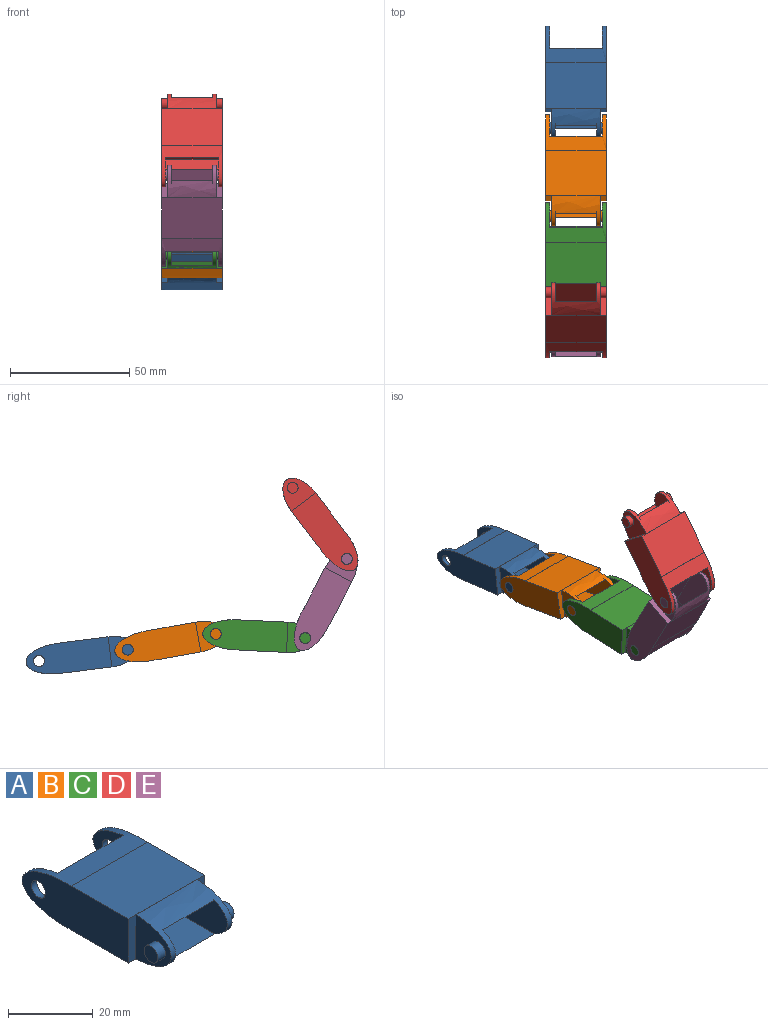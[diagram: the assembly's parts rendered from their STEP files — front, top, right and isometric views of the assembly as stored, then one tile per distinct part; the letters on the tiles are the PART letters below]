
ASSEMBLY  parts=5 mates=4
PART A: 27 faces, bbox 25.4x47.1x12.7 mm
  f0: plane 32.73x21.87mm, normal (0,0,-1), area 623.3mm2, adj f1,f3,f14,f15,f23,f24,f25,f26
  f1: plane 22.74x12.12mm, normal (1,0,0), area 196.9mm2, adj f0,f2,f7,f12,f13,f14,f26
  f2: plane 32.73x21.87mm, normal (0,0,1), area 623.3mm2, adj f1,f3,f13,f15,f23,f24,f25,f26
  f3: plane 22.74x12.12mm, normal (-1,0,0), area 196.9mm2, adj f0,f2,f6,f12,f13,f14,f25
  f4: plane 25.4x0.06mm, normal (0,1,0), area 1.6mm2, adj f9,f10,f11,f12
  f5: plane 25.4x0.06mm, normal (0,1,0), area 1.6mm2, adj f8,f9,f11,f12
  f6: cylinder r=2.3mm len=4.61mm, axis (1,0,0), area 25.5mm2, adj f3,f9
  f7: cylinder r=2.3mm len=4.61mm, axis (1,0,0), area 25.5mm2, adj f1,f11
  f8: plane 25.4x19.05mm, normal (0,0,1), area 483.9mm2, adj f5,f9,f11,f16
  f9: plane 35.44x12.7mm, normal (1,0,0), area 394.1mm2, adj f4,f5,f6,f8,f10,f12,f16
  f10: plane 25.4x19.05mm, normal (0,0,-1), area 483.9mm2, adj f4,f9,f11,f16
  f11: plane 35.44x12.7mm, normal (-1,0,0), area 394.1mm2, adj f4,f5,f7,f8,f10,f12,f16
  f12: extruded ~25.4x16.39mm, area 409.4mm2, adj f1,f3,f4,f5,f9,f11,f13,f14
  f13: plane 21.87x1.17mm, normal (0,1,0), area 25.6mm2, adj f1,f2,f3,f12
  f14: plane 21.87x1.17mm, normal (0,1,0), area 25.6mm2, adj f0,f1,f3,f12
  f15: extruded ~20.32x12.7mm, area 349.8mm2, adj f0,f2,f16,f17,f18,f23,f24
  f16: plane 25.4x12.7mm, normal (0,-1,0), area 64.6mm2, adj f8,f9,f10,f11,f15,f17,f18
  f17: plane 12.7x11.7mm, normal (1,0,0), area 99.9mm2, adj f15,f16,f21
  f18: plane 12.7x11.7mm, normal (-1,0,0), area 99.9mm2, adj f15,f16,f20
  f19: plane 4.55x4.55mm, normal (-1,0,0), area 16.2mm2, adj f20
  f20: cylinder r=2.27mm len=4.55mm, axis (1,0,0), area 36.3mm2, adj f18,f19
  f21: cylinder r=2.27mm len=4.55mm, axis (1,0,0), area 36.3mm2, adj f17,f22
  f22: plane 4.55x4.55mm, normal (1,0,0), area 16.2mm2, adj f21
  f23: plane 24.4x9.79mm, normal (1,0,0), area 225.9mm2, adj f0,f2,f15,f26
  f24: plane 24.4x9.79mm, normal (-1,0,0), area 225.9mm2, adj f0,f2,f15,f25
  f25: plane 9.79x2.3mm, normal (0,1,0), area 22.5mm2, adj f0,f2,f3,f24
  f26: plane 9.79x2.3mm, normal (0,1,0), area 22.5mm2, adj f0,f1,f2,f23
PART B: same geometry as A
PART C: same geometry as A
PART D: same geometry as A
PART E: same geometry as A
PLACE A rot(axis=(-1,0,0),7.3deg) t=(83.35,91.42,40.24)mm
PLACE B rot(axis=(-1,0,0),10.1deg) t=(83.35,54.35,45.84)mm
PLACE C rot(axis=(1,0,0),2.7deg) t=(83.35,17.17,48.57)mm
PLACE D rot(axis=(-1,0,0),127.3deg) t=(83.35,-10.04,94.54)mm
PLACE E rot(axis=(-1,0,0),62.3deg) t=(83.35,-11.08,62.89)mm
MATE revolute E.f20 <-> D.f6  axis (1,0,0) through (96.05,-20.5,80.82)mm
MATE revolute C.f20 <-> E.f6  axis (1,0,0) through (96.05,-3.06,47.61)mm
MATE revolute A.f20 <-> B.f6  axis (1,0,0) through (96.05,71.33,42.81)mm
MATE revolute B.f20 <-> C.f6  axis (1,0,0) through (96.05,34.4,49.39)mm
